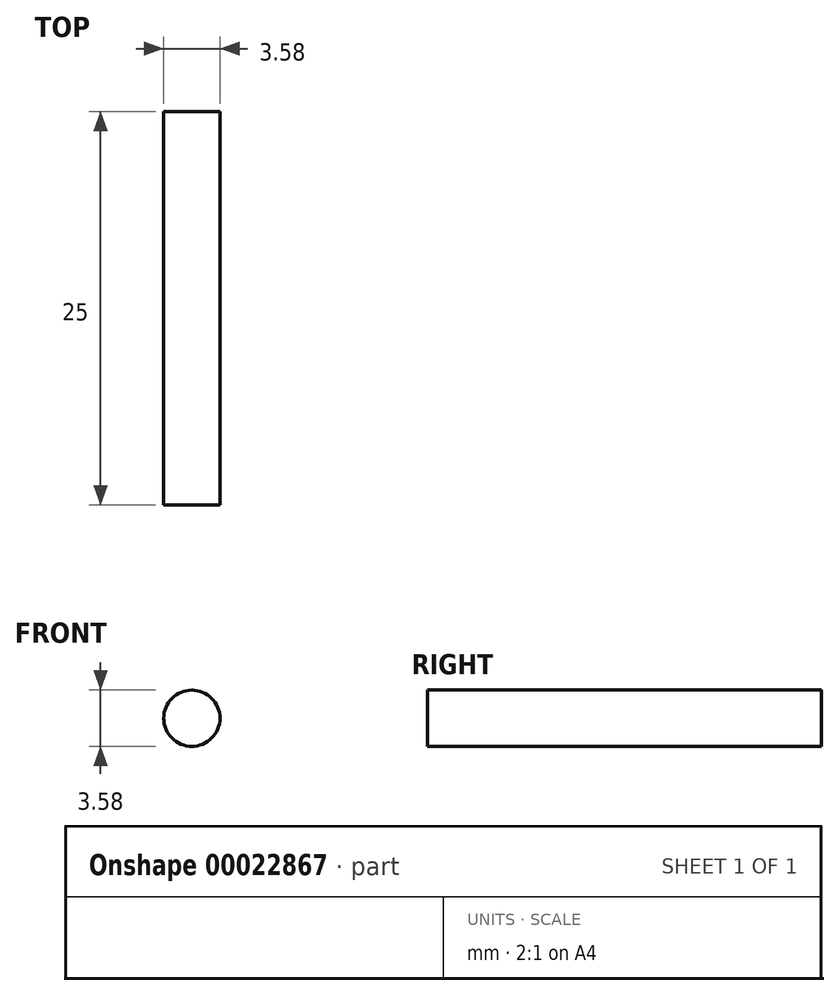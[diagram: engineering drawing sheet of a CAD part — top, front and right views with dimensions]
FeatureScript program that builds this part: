
annotation { "Feature Type Name" : "Feature", "Feature Type Description" : "" }
export const myFeature = defineFeature(function(context is Context, id is Id, definition is map)
    precondition{}
    {
        {
            var Q0;
            Q0=qCreatedBy(makeId("Front.planeOp"),FACE);
            var sketch = newSketch(context, id + "F0", { "sketchPlane" : qUnion([Q0])});
            skCircle(sketch, "E0", {"center": v(0, 0) * mm, "radius": 1.79 * mm});
            skSolve(sketch);
        }
        {
            var Q0;
            Q0=makeQuery(id+"F0.imprint","IMPRINT",FACE,{"disambiguationData":[TD([[makeQuery(id+"F0.imprint","IMPRINT",EDGE,{"derivedFrom":sQuery(id+"F0.wireOp",EDGE,"E0")}),1.0]])]});
            extrude(context, id + "F1", {"entities" : qUnion([Q0]), "depth" : 25 * mm});
        }
    });
